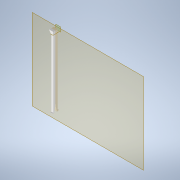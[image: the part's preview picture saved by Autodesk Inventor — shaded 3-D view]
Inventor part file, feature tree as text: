
AUTODESK INVENTOR PART (.ipt)
format: ipt  version: 2021.3 (Build 253353010, 353A)  size: 203,264 bytes
history: native  units: mm
features: reference x8, extrude x4, fillet x4, sketch x4, plane x3, other x3, projected_geometry x1
ambient origin geometry x8: Origin, YZ Plane, XZ Plane, XY Plane, X Axis, Y Axis, Z Axis, Center Point
bodies: Volumenkörper1 (feature_tree)
feature tree (27):
  plane  "Arbeitsebene1"
  plane  "Arbeitsebene2"
  extrude  "Extrusion1"  Depth=5.0mm TaperAngle=0.0deg
  plane  "Arbeitsebene3"
  extrude  "Extrusion2"  Depth=0.1mm
  extrude  "Extrusion3"  Depth=1.5mm
  extrude  "Extrusion4"  Depth=0.1mm TaperAngle=0.0deg
  fillet  "Rundung1"  Radius=3.0mm
  fillet  "Rundung2"  Radius=1.0mm
  fillet  "Rundung3"  Radius=73.0mm
  fillet  "Rundung4"  Radius=0.5mm
  sketch  "Skizze2"  dims[d1=3.0mm d2=5.0mm d3=0.0mm]
  reference  "Referenz1"
  reference  "Referenz2"
  reference  "Referenz3"
  sketch  "Skizze3"  dims[d4=0.0mm d6=0.1mm]
  reference  "Referenz8"
  reference  "Referenz9"
  reference  "Referenz10"
  projected_geometry  "Projizierte Kontur2"
  reference  "Referenz11"
  sketch  "Skizze4"  dims[d8=72.0mm d9=0.0mm d10=1.5mm]
  sketch  "Skizze5"  dims[d13=1.5mm d14=73.0mm d15=0.0mm d16=3.0mm d18=1.0mm d19=73.0mm d20=0.0mm d22=0.5mm d23=0.2mm d24=0.1mm d25=0.5mm d26=0.2mm d27=0.2mm d28=0.1mm d29=7.0mm]
  reference  "Referenz13"
  other  "<userpath>\Documents\Inventor\MotorController\gehaeuse_bg.iam"
  other  "gehaeuse_bg.iam"
  other  "gehause:1"
